# Revit family: EL_Durga_2
name_source: partatom
category: Lighting Fixtures
units: mm (PartAtom-declared; Revit-internal decimal feet)

## family parameters
Always vertical = Yes
Cut with Voids When Loaded = No
Light Source = Yes
Maintain Annotation Orientation = No
OmniClass Number = 23.80.70.00
OmniClass Title = Lighting
Part Type = Normal
Room Calculation Point = No
Round Connector Dimension = Use Diameter
Shared = No
Work Plane-Based = No

## types (12) — shared parameters
CE Conformity = CE Mark
CRI = 70
Color Filter = 16777215
Control Gear = LED Driver
Default Elevation = 1500 mm
Description = Street luminaire
Diffuser Material  = Flat glass
Dimming Lamp Color Temperature Shift = <None>
EL_Voltage = AC 220V - 240V / 50-60Hz
Emit from Line Length = 610 mm
Housing Height = 91 mm  [stored 0.298556 ft]
Housing Width = 228 mm  [stored 0.748031 ft]
IK = IK10
IP = IP66
Lamp = LED
Life Time = 100 000 h
Light Source Symbol Length = 3048 mm  [stored 10 ft]
Luminaire Material = Kov
Manufacturer = ELEKTRO-LUMEN, s. r. o.
Optical Efficacy = 75.5
Spot Beam Angle = 30.00°
Spot Field Angle = 90.00°
Terminal Block Poles = 2, 3, 5
Tilt Angle = 90.00°
URL Luminaire = https://www.el-lumen.cz
URL Manufacturer = https://www.el-lumen.cz
Voltage  = AC 220V - 240V / 50-60Hz

## per-type parameters (varying)
| type | CCT | Housing Length | Luminaire Type | Luminous Flux of LED | Luminous Flux of Luminaire | Model | Power | Weight |
| DURGA 4 G2  12k0 740 | 4000 | 1070 mm  [stored 3.5105 ft] | DURGA 4 G2 | 12000 lm | 9060 lm | DURGA 4 G2 | 64 W | 10.6 |
| DURGA 4 G2  10k0 740 | 4000 | 1070 mm  [stored 3.5105 ft] | DURGA 4 G2 | 10000 lm | 7550 lm | DURGA 4 G2 | 53 W | 10.6 |
| DURGA 4 G2  8k0 740 | 4000 | 1070 mm  [stored 3.5105 ft] | DURGA 4 G2 | 8000 lm | 6040 lm | DURGA 4 G2 | 42 W | 10.6 |
| DURGA 4 G2  12k0 730 | 3000 | 1070 mm  [stored 3.5105 ft] | DURGA 4 G2 | 12000 lm | 9060 lm | DURGA 4 G2 | 68 W | 10.6 |
| DURGA 4 G2  10k0 730 | 3000 | 1070 mm  [stored 3.5105 ft] | DURGA 4 G2 | 10000 lm | 7550 lm | DURGA 4 G2 | 56 W | 10.6 |
| DURGA 4 G2  8k0 730 | 3000 | 1070 mm  [stored 3.5105 ft] | DURGA 4 G2 | 8000 lm | 6040 lm | DURGA 4 G2 | 44 W | 10.6 |
| DURGA 3 G2  6k0 740 | 4000 | 835 mm  [stored 2.7395 ft] | DURGA 3 G2 | 6000 lm | 4530 lm | DURGA 3 G2 | 32 W | 8.2 |
| DURGA 3 G2  4k0 740 | 4000 | 835 mm  [stored 2.7395 ft] | DURGA 3 G2 | 4000 lm | 3020 lm | DURGA 3 G2 | 21 W | 8.2 |
| DURGA 3 G2  2k0 740 | 4000 | 835 mm  [stored 2.7395 ft] | DURGA 3 G2 | 2000 lm | 1510 lm | DURGA 3 G2 | 14 W | 8.2 |
| DURGA 3 G2  6k0 730 | 3000 | 835 mm  [stored 2.7395 ft] | DURGA 3 G2 | 6000 lm | 4530 lm | DURGA 3 G2 | 34 W | 8.2 |
| DURGA 3 G2  4k0 730 | 3000 | 835 mm  [stored 2.7395 ft] | DURGA 3 G2 | 4000 lm | 3020 lm | DURGA 3 G2 | 22 W | 8.2 |
| DURGA 3 G2  2k0 730 | 3000 | 835 mm  [stored 2.7395 ft] | DURGA 3 G2 | 2000 lm | 1510 lm | DURGA 3 G2 | 15 W | 8.2 |

note: column(s) folded — value = type name in every type: Luminaire Model

note: [stored X ft] marks values corroborated as IEEE doubles in the binary element streams (Revit-internal decimal feet)
